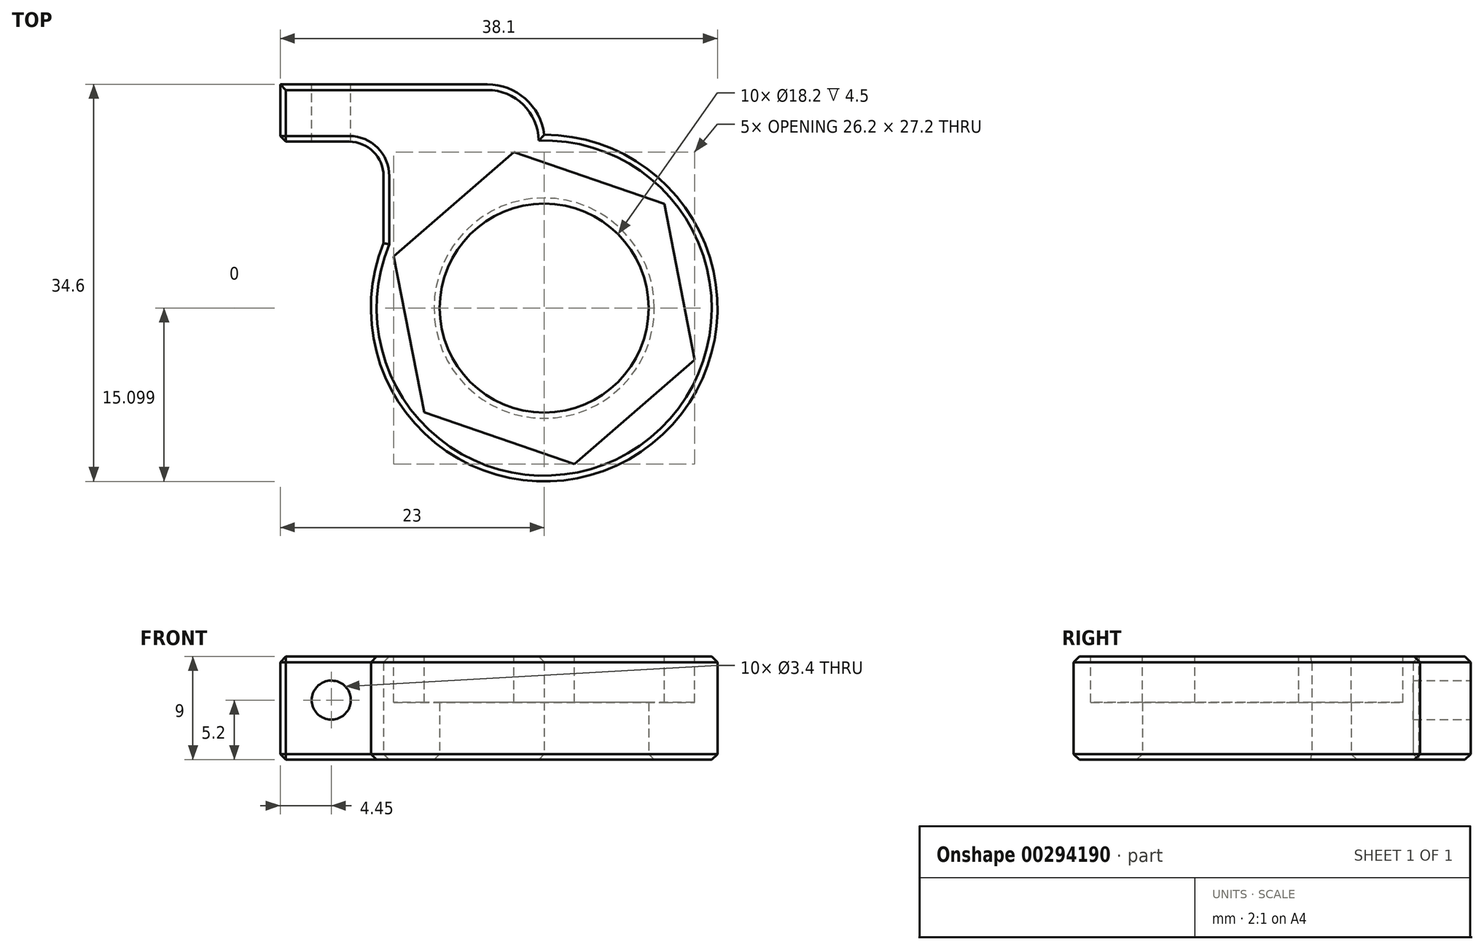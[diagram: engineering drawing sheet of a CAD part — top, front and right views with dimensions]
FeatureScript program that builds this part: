
annotation { "Feature Type Name" : "Feature", "Feature Type Description" : "" }
export const myFeature = defineFeature(function(context is Context, id is Id, definition is map)
    precondition{}
    {
        {
            var Q0;
            Q0=qCreatedBy(makeId("Top.planeOp"),FACE);
            var sketch = newSketch(context, id + "F0", { "sketchPlane" : qUnion([Q0])});
            skCircle(sketch, "E0", {"center": v(0, -0.44) * mm, "radius": 9.1 * mm});
            skArc(sketch, "E1.0", {"start": v(-14, 5.22) * mm, "mid": v(8.44, -12.96) * mm, "end": v(0, 14.66) * mm});
            skLineSegment(sketch, "E2", {"start": v(0, 0) * mm, "end": v(0, 7.86) * mm, "construction": true});
            skLineSegment(sketch, "E3", {"start": v(0, 0) * mm, "end": v(19.76, 0) * mm, "construction": true});
            skLineSegment(sketch, "E4", {"start": v(-14, 11.06) * mm, "end": v(-14, 5.22) * mm});
            skLineSegment(sketch, "E5.MirrorCS", {"start": v(-4.96, 19.06) * mm, "end": v(-23, 19.06) * mm});
            skLineSegment(sketch, "E6.MirrorCS", {"start": v(-23, 19.06) * mm, "end": v(-23, 14.06) * mm});
            skLineSegment(sketch, "E7", {"start": v(0, 14.66) * mm, "end": v(0, 14.66) * mm});
            skPoint(sketch, "E7.startSnap0", {"position": v(0, 3.93) * mm});
            skLineSegment(sketch, "E8", {"start": v(-17, 14.06) * mm, "end": v(-23, 14.06) * mm});
            skPoint(sketch, "E9.visualSharp", {"position": v(0, 19.06) * mm});
            skArc(sketch, "E9.filletArc", {"start": v(0, 14.66) * mm, "mid": v(-1.65, 17.8) * mm, "end": v(-4.96, 19.06) * mm});
            skPoint(sketch, "E10.visualSharp", {"position": v(-14, 14.06) * mm});
            skArc(sketch, "E10.filletArc", {"start": v(-14, 11.06) * mm, "mid": v(-14.88, 13.18) * mm, "end": v(-17, 14.06) * mm});
            skLineSegment(sketch, "E11", {"start": v(0, -0.44) * mm, "end": v(-30.2, -0.44) * mm, "construction": true});
            skLineSegment(sketch, "E12", {"start": v(-15.1, -0.44) * mm, "end": v(-15.1, -25.6) * mm, "construction": true});
            skLineSegment(sketch, "E13", {"start": v(-15.1, -25.6) * mm, "end": v(-15.1, -14.97) * mm, "construction": true});
            skLineSegment(sketch, "E14", {"start": v(0, -25.14) * mm, "end": v(0, 33.27) * mm, "construction": true});
            skSolve(sketch);
        }
        {
            var Q0;
            Q0=makeQuery(id+"F0.imprint","IMPRINT",FACE,{"disambiguationData":[TD([[makeQuery(id+"F0.imprint","IMPRINT",EDGE,{"derivedFrom":sQuery(id+"F0.wireOp",EDGE,"E0")}),-1.0]])]});
            extrude(context, id + "F1", {"entities" : qUnion([Q0]), "depth" : 9 * mm});
        }
        {
            var Q0;
            Q0=makeQuery(id+"F1.opExtrude","CAP_FACE",FACE,{"disambiguationData":[OSD([sQuery(id+"F0.wireOp",EDGE,"E0"),sQuery(id+"F0.wireOp",EDGE,"E1.0"),sQuery(id+"F0.wireOp",EDGE,"E4"),sQuery(id+"F0.wireOp",EDGE,"2b91ec16-6f3c-470a-ac91-a327bda2e9c00.MirrorCS"),sQuery(id+"F0.wireOp",EDGE,"E5.MirrorCS"),sQuery(id+"F0.wireOp",EDGE,"E6.MirrorCS"),sQuery(id+"F0.wireOp",EDGE,"E7"),sQuery(id+"F0.wireOp",EDGE,"E8")])],"isStart":true});
            var Q1;
            Q1=makeQuery(id+"F1.opExtrude","CAP_EDGE",EDGE,{"disambiguationData":[OSD([sQuery(id+"F0.wireOp",EDGE,"E1.0")])],"isStart":false});
            var Q2;
            Q2=makeQuery(id+"F1.opExtrude","CAP_EDGE",EDGE,{"disambiguationData":[OSD([sQuery(id+"F0.wireOp",EDGE,"E4")])],"isStart":false});
            var Q3;
            Q3=makeQuery(id+"F1.opExtrude","CAP_EDGE",EDGE,{"disambiguationData":[OSD([sQuery(id+"F0.wireOp",EDGE,"E8")])],"isStart":false});
            var Q4;
            Q4=makeQuery(id+"F1.opExtrude","CAP_EDGE",EDGE,{"disambiguationData":[OSD([sQuery(id+"F0.wireOp",EDGE,"E10.filletArc")])],"isStart":false});
            var Q5;
            Q5=makeQuery(id+"F1.opExtrude","CAP_EDGE",EDGE,{"disambiguationData":[OSD([sQuery(id+"F0.wireOp",EDGE,"E6.MirrorCS")])],"isStart":false});
            var Q6;
            Q6=makeQuery(id+"F1.opExtrude","CAP_EDGE",EDGE,{"disambiguationData":[OSD([sQuery(id+"F0.wireOp",EDGE,"E5.MirrorCS")])],"isStart":false});
            var Q7;
            Q7=makeQuery(id+"F1.opExtrude","CAP_EDGE",EDGE,{"disambiguationData":[OSD([sQuery(id+"F0.wireOp",EDGE,"E9.filletArc")])],"isStart":false});
            var Q8;
            Q8=makeQuery(id+"F1.opExtrude","CAP_EDGE",EDGE,{"disambiguationData":[OSD([sQuery(id+"F0.wireOp",EDGE,"700c368e-82d3-4afa-9ae0-bb0f28912ef30.MirrorCS")])],"isStart":false});
            var Q9;
            Q9=makeQuery(id+"F1.opExtrude","SWEPT_EDGE",EDGE,{"disambiguationData":[OSD([sQuery(id+"F0.wireOp",EDGE,"E6.MirrorCS"),sQuery(id+"F0.wireOp",EDGE,"E8")])]});
            chamfer(context, id + "F2", {"entities" : qUnion([Q0, Q1, Q2, Q3, Q4, Q5, Q6, Q7, Q8, Q9]), "width" : 0.5 * mm, "tangentPropagation" : true});
        }
        {
            var Q0;
            Q0=makeQuery(id+"F1.opExtrude","SWEPT_FACE",FACE,{"disambiguationData":[OSD([sQuery(id+"F0.wireOp",EDGE,"E5.MirrorCS")])]});
            var sketch = newSketch(context, id + "F3", { "sketchPlane" : qUnion([Q0])});
            skCircle(sketch, "E15", {"center": v(18.55, 5.2) * mm, "radius": 1.7 * mm});
            skSolve(sketch);
        }
        {
            var Q0;
            Q0=makeQuery(id+"F3.imprint","IMPRINT",FACE,{"disambiguationData":[TD([[makeQuery(id+"F3.imprint","IMPRINT",EDGE,{"derivedFrom":sQuery(id+"F3.wireOp",EDGE,"E15")}),1.0]])]});
            extrude(context, id + "F4", {"entities" : qUnion([Q0]), "operationType" : NewBodyOperationType.REMOVE, "endBound" : BoundingType.UP_TO_NEXT, "oppositeDirection" : true, "depth" : 25 * mm});
        }
        {
            var Q0;
            Q0=makeQuery(id+"F1.opExtrude","CAP_FACE",FACE,{"disambiguationData":[OSD([sQuery(id+"F0.wireOp",EDGE,"E0"),sQuery(id+"F0.wireOp",EDGE,"E1.0"),sQuery(id+"F0.wireOp",EDGE,"E4"),sQuery(id+"F0.wireOp",EDGE,"2b91ec16-6f3c-470a-ac91-a327bda2e9c00.MirrorCS"),sQuery(id+"F0.wireOp",EDGE,"E5.MirrorCS"),sQuery(id+"F0.wireOp",EDGE,"E6.MirrorCS"),sQuery(id+"F0.wireOp",EDGE,"E7"),sQuery(id+"F0.wireOp",EDGE,"E8")])],"isStart":false});
            var sketch = newSketch(context, id + "F5", { "sketchPlane" : qUnion([Q0])});
            skPoint(sketch, "E16.0", {"position": v(0, -0.44) * mm});
            skCircle(sketch, "E17.cCircle", {"center": v(0, -0.44) * mm, "radius": 12 * mm, "construction": true});
            skLineSegment(sketch, "E17.0", {"start": v(2.64, -14.04) * mm, "end": v(-10.46, -9.53) * mm});
            skLineSegment(sketch, "E17.1", {"start": v(-10.46, -9.53) * mm, "end": v(-13.1, 4.07) * mm});
            skLineSegment(sketch, "E17.2", {"start": v(-13.1, 4.07) * mm, "end": v(-2.64, 13.16) * mm});
            skLineSegment(sketch, "E17.3", {"start": v(-2.64, 13.16) * mm, "end": v(10.46, 8.65) * mm});
            skLineSegment(sketch, "E17.4", {"start": v(10.46, 8.65) * mm, "end": v(13.1, -4.95) * mm});
            skLineSegment(sketch, "E17.5", {"start": v(13.1, -4.95) * mm, "end": v(2.64, -14.04) * mm});
            skPoint(sketch, "E17.0.midPoint", {"position": v(-3.9, -11.79) * mm});
            skSolve(sketch);
        }
        {
            var Q0;
            Q0=makeQuery(id+"F5.imprint","IMPRINT",FACE,{"disambiguationData":[TD([[makeQuery(id+"F5.imprint","IMPRINT",EDGE,{"derivedFrom":sQuery(id+"F5.wireOp",EDGE,"E17.0")}),-1.0]])]});
            extrude(context, id + "F6", {"entities" : qUnion([Q0]), "operationType" : NewBodyOperationType.REMOVE, "oppositeDirection" : true, "depth" : 4 * mm});
        }
    });
